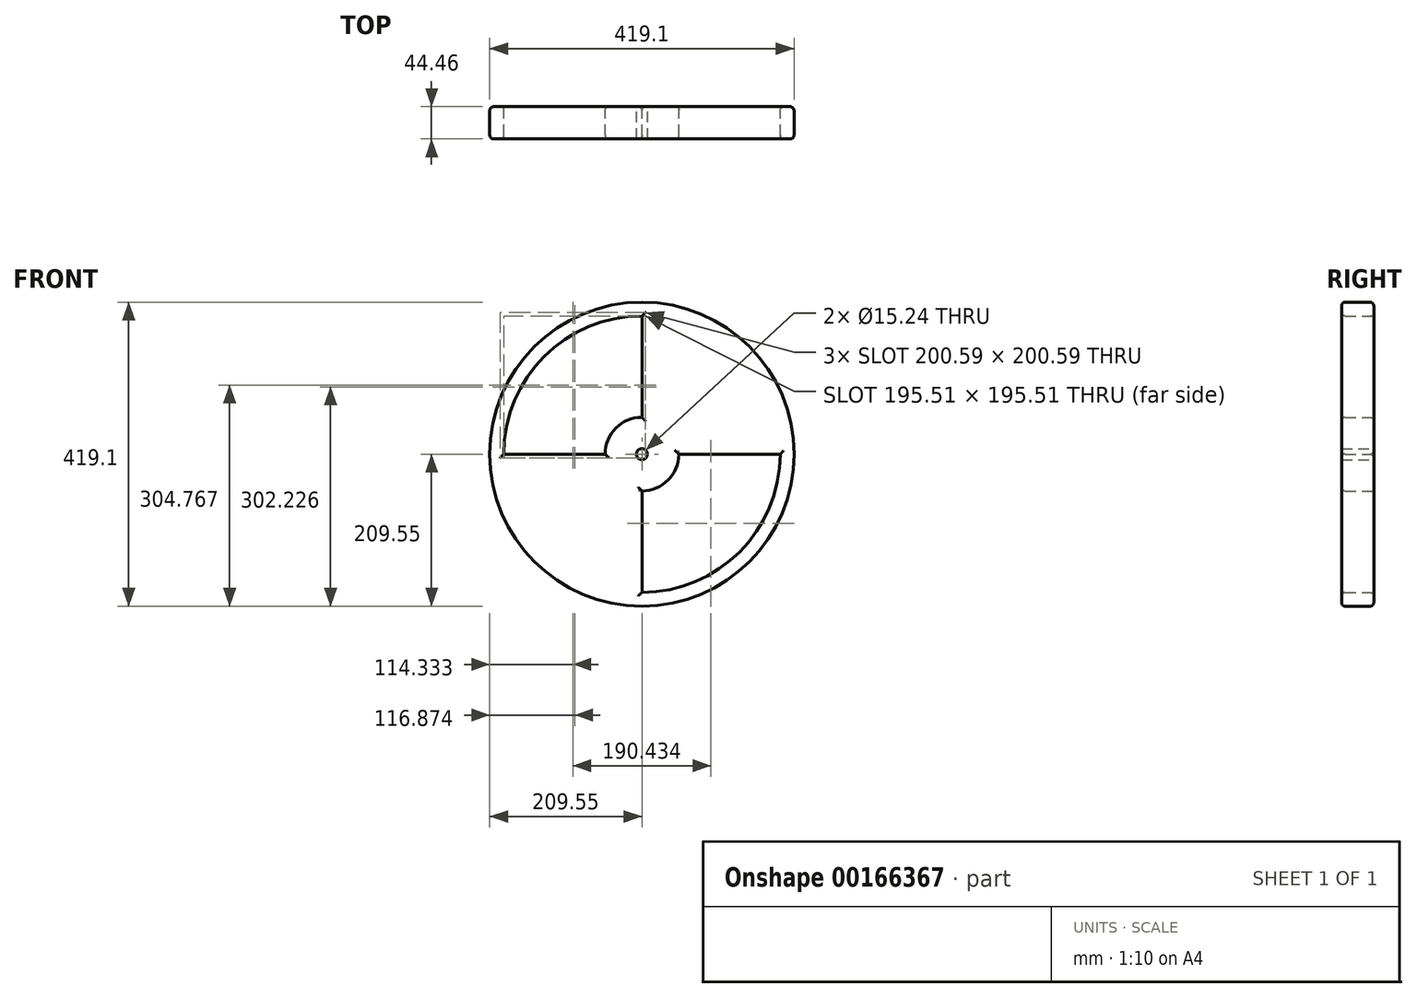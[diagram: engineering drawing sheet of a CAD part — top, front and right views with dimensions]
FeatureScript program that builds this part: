
annotation { "Feature Type Name" : "Feature", "Feature Type Description" : "" }
export const myFeature = defineFeature(function(context is Context, id is Id, definition is map)
    precondition{}
    {
        {
            var Q0;
            Q0=qCreatedBy(makeId("Front.planeOp"),FACE);
            var sketch = newSketch(context, id + "F0", { "sketchPlane" : qUnion([Q0])});
            skCircle(sketch, "E0", {"center": v(0, 0) * mm, "radius": 7.62 * mm});
            skCircle(sketch, "E1", {"center": v(0, 0) * mm, "radius": 50.8 * mm});
            skCircle(sketch, "E2", {"center": v(0, 0) * mm, "radius": 190.5 * mm});
            skCircle(sketch, "E3", {"center": v(0, 0) * mm, "radius": 209.55 * mm});
            skLineSegment(sketch, "E4", {"start": v(0, -190.5) * mm, "end": v(0, -50.8) * mm});
            skLineSegment(sketch, "E5", {"start": v(-190.5, 0) * mm, "end": v(-50.8, 0) * mm});
            skLineSegment(sketch, "E6", {"start": v(0, 7.62) * mm, "end": v(0, 0) * mm});
            skPoint(sketch, "E7.MirrorCS.end.orphan", {"position": v(0, 7.62) * mm});
            skPoint(sketch, "E7.MirrorCS.start.orphan", {"position": v(0, 50.8) * mm});
            skPoint(sketch, "E8.end.orphan", {"position": v(0, -7.62) * mm});
            skLineSegment(sketch, "E9", {"start": v(0, 50.8) * mm, "end": v(0, 190.5) * mm});
            skLineSegment(sketch, "E10", {"start": v(50.8, 0) * mm, "end": v(190.5, 0) * mm});
            skSolve(sketch);
        }
        {
            var Q0;
            Q0 = qSketchRegion(id + "F0", true);
            var Q1;
            Q1=makeQuery(id+"F0.imprint","IMPRINT",FACE,{"disambiguationData":[TD([[makeQuery(id+"F0.imprint","IMPRINT",EDGE,{"derivedFrom":sQuery(id+"F0.wireOp",EDGE,"E0")}),-1.0]])]});
            var Q2;
            {var subQ0=sQuery(id+"F0.wireOp",EDGE,"E4");Q2=makeQuery(id+"F0.imprint","IMPRINT",FACE,{"disambiguationData":[TD([[makeQuery(id+"F0.imprint","IMPRINT",EDGE,{"derivedFrom":subQ0}),1.0]])]});}
            var Q3;
            {var subQ0=sQuery(id+"F0.wireOp",EDGE,"E9");Q3=makeQuery(id+"F0.imprint","IMPRINT",FACE,{"disambiguationData":[TD([[makeQuery(id+"F0.imprint","IMPRINT",EDGE,{"derivedFrom":subQ0}),-1.0]])]});}
            extrude(context, id + "F1", {"entities" : qUnion([Q0, Q1, Q2, Q3]), "endBound" : BoundingType.SYMMETRIC, "depth" : 44.45 * mm});
        }
        {
            var Q0;
            Q0=makeQuery(id+"F1.opExtrude","CAP_EDGE",EDGE,{"disambiguationData":[OSD([sQuery(id+"F0.wireOp",EDGE,"E3")])],"isStart":false});
            var Q1;
            {var subQ0=sQuery(id+"F0.wireOp",EDGE,"E1");Q1=makeQuery(id+"F1.opExtrude","CAP_EDGE",EDGE,{"disambiguationData":[OSD([subQ0]),TDD([makeQuery(id+"F0.imprint","IMPRINT",EDGE,{"disambiguationData":[TD([[makeQuery(id+"F0.imprint","INTERSECT",VERTEX,{"derivedFrom":[subQ0,sQuery(id+"F0.wireOp",EDGE,"E5")]}),1.0]])],"derivedFrom":subQ0})])],"isStart":false});}
            var Q2;
            {var subQ0=sQuery(id+"F0.wireOp",EDGE,"E1");Q2=makeQuery(id+"F1.opExtrude","CAP_EDGE",EDGE,{"disambiguationData":[OSD([subQ0]),TDD([makeQuery(id+"F0.imprint","IMPRINT",EDGE,{"disambiguationData":[TD([[makeQuery(id+"F0.imprint","INTERSECT",VERTEX,{"derivedFrom":[subQ0,sQuery(id+"F0.wireOp",EDGE,"E4")]}),-1.0]])],"derivedFrom":subQ0})])],"isStart":false});}
            var Q3;
            {var subQ0=sQuery(id+"F0.wireOp",EDGE,"E2");Q3=makeQuery(id+"F1.opExtrude","CAP_EDGE",EDGE,{"disambiguationData":[OSD([subQ0]),TDD([makeQuery(id+"F0.imprint","IMPRINT",EDGE,{"disambiguationData":[TD([[makeQuery(id+"F0.imprint","INTERSECT",VERTEX,{"derivedFrom":[subQ0,sQuery(id+"F0.wireOp",EDGE,"E4")]}),-1.0]])],"derivedFrom":subQ0})])],"isStart":false});}
            var Q4;
            {var subQ0=sQuery(id+"F0.wireOp",EDGE,"E2");Q4=makeQuery(id+"F1.opExtrude","CAP_EDGE",EDGE,{"disambiguationData":[OSD([subQ0]),TDD([makeQuery(id+"F0.imprint","IMPRINT",EDGE,{"disambiguationData":[TD([[makeQuery(id+"F0.imprint","INTERSECT",VERTEX,{"derivedFrom":[subQ0,sQuery(id+"F0.wireOp",EDGE,"E4")]}),-1.0]])],"derivedFrom":subQ0})])],"isStart":true});}
            var Q5;
            {var subQ0=sQuery(id+"F0.wireOp",EDGE,"E2");Q5=makeQuery(id+"F1.opExtrude","CAP_EDGE",EDGE,{"disambiguationData":[OSD([subQ0]),TDD([makeQuery(id+"F0.imprint","IMPRINT",EDGE,{"disambiguationData":[TD([[makeQuery(id+"F0.imprint","INTERSECT",VERTEX,{"derivedFrom":[subQ0,sQuery(id+"F0.wireOp",EDGE,"E5")]}),1.0]])],"derivedFrom":subQ0})])],"isStart":false});}
            var Q6;
            Q6=makeQuery(id+"F1.opExtrude","CAP_EDGE",EDGE,{"disambiguationData":[OSD([sQuery(id+"F0.wireOp",EDGE,"E3")])],"isStart":true});
            var Q7;
            {var subQ0=sQuery(id+"F0.wireOp",EDGE,"E1");Q7=makeQuery(id+"F1.opExtrude","CAP_EDGE",EDGE,{"disambiguationData":[OSD([subQ0]),TDD([makeQuery(id+"F0.imprint","IMPRINT",EDGE,{"disambiguationData":[TD([[makeQuery(id+"F0.imprint","INTERSECT",VERTEX,{"derivedFrom":[subQ0,sQuery(id+"F0.wireOp",EDGE,"E5")]}),1.0]])],"derivedFrom":subQ0})])],"isStart":true});}
            var Q8;
            Q8=makeQuery(id+"F1.opExtrude","CAP_EDGE",EDGE,{"disambiguationData":[OSD([sQuery(id+"F0.wireOp",EDGE,"E9")])],"isStart":true});
            var Q9;
            Q9=makeQuery(id+"F1.opExtrude","CAP_EDGE",EDGE,{"disambiguationData":[OSD([sQuery(id+"F0.wireOp",EDGE,"E10")])],"isStart":true});
            var Q10;
            Q10=makeQuery(id+"F1.opExtrude","CAP_EDGE",EDGE,{"disambiguationData":[OSD([sQuery(id+"F0.wireOp",EDGE,"E5")])],"isStart":true});
            fillet(context, id + "F2", {"entities" : qUnion([Q0, Q1, Q2, Q3, Q4, Q5, Q6, Q7, Q8, Q9, Q10]), "radius" : 5.08 * mm, "tangentPropagation" : true, "allowEdgeOverflow" : false});
        }
        {
            var Q0;
            Q0=makeQuery(id+"F1.opExtrude","CAP_EDGE",EDGE,{"disambiguationData":[OSD([sQuery(id+"F0.wireOp",EDGE,"E4")])],"isStart":false});
            var Q1;
            Q1=makeQuery(id+"F1.opExtrude","CAP_EDGE",EDGE,{"disambiguationData":[OSD([sQuery(id+"F0.wireOp",EDGE,"E4")])],"isStart":true});
            var Q2;
            Q2=makeQuery(id+"F1.opExtrude","CAP_EDGE",EDGE,{"disambiguationData":[OSD([sQuery(id+"F0.wireOp",EDGE,"E10")])],"isStart":false});
            var Q3;
            Q3=makeQuery(id+"F1.opExtrude","CAP_EDGE",EDGE,{"disambiguationData":[OSD([sQuery(id+"F0.wireOp",EDGE,"E5")])],"isStart":false});
            var Q4;
            Q4=makeQuery(id+"F1.opExtrude","CAP_EDGE",EDGE,{"disambiguationData":[OSD([sQuery(id+"F0.wireOp",EDGE,"E9")])],"isStart":false});
            fillet(context, id + "F3", {"entities" : qUnion([Q0, Q1, Q2, Q3, Q4]), "radius" : 5.08 * mm, "tangentPropagation" : true, "allowEdgeOverflow" : false});
        }
    });
